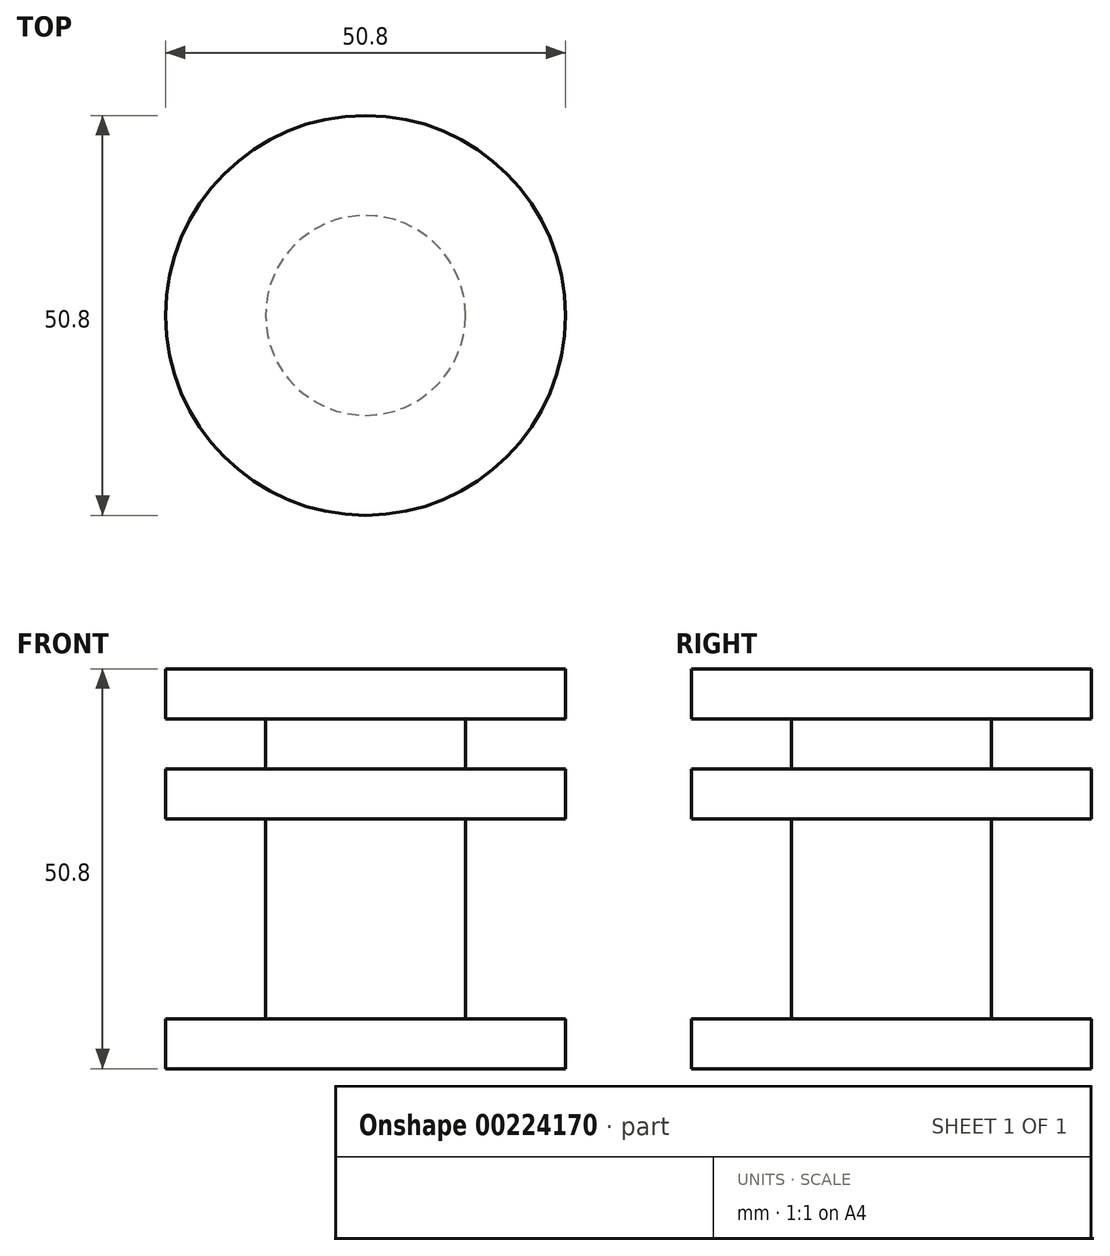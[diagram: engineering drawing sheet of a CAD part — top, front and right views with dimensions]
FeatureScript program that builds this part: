
annotation { "Feature Type Name" : "Feature", "Feature Type Description" : "" }
export const myFeature = defineFeature(function(context is Context, id is Id, definition is map)
    precondition{}
    {
        {
            var Q0;
            Q0=qCreatedBy(makeId("Front.planeOp"),FACE);
            var sketch = newSketch(context, id + "F0", { "sketchPlane" : qUnion([Q0])});
            skLineSegment(sketch, "E0", {"start": v(0, 0) * mm, "end": v(0, 47.13) * mm, "construction": true});
            skLineSegment(sketch, "E1", {"start": v(12.7, 0) * mm, "end": v(12.7, -25.4) * mm});
            skLineSegment(sketch, "E2", {"start": v(0, -25.4) * mm, "end": v(0, 0) * mm});
            skLineSegment(sketch, "E3", {"start": v(12.7, 0) * mm, "end": v(25.4, 0) * mm});
            skLineSegment(sketch, "E4", {"start": v(25.4, 0) * mm, "end": v(25.4, 6.35) * mm});
            skLineSegment(sketch, "E5", {"start": v(25.4, 6.35) * mm, "end": v(12.7, 6.35) * mm});
            skLineSegment(sketch, "E6", {"start": v(12.7, 6.35) * mm, "end": v(12.7, 12.7) * mm});
            skLineSegment(sketch, "E7", {"start": v(12.7, 12.7) * mm, "end": v(25.4, 12.7) * mm});
            skLineSegment(sketch, "E8", {"start": v(25.4, 12.7) * mm, "end": v(25.4, 19.05) * mm});
            skLineSegment(sketch, "E9", {"start": v(25.4, 19.05) * mm, "end": v(0, 19.05) * mm});
            skLineSegment(sketch, "E10", {"start": v(0, 19.05) * mm, "end": v(0, 0) * mm});
            skLineSegment(sketch, "E11", {"start": v(12.7, -25.4) * mm, "end": v(25.4, -25.4) * mm});
            skLineSegment(sketch, "E12", {"start": v(25.4, -25.4) * mm, "end": v(25.4, -31.75) * mm});
            skLineSegment(sketch, "E13", {"start": v(25.4, -31.75) * mm, "end": v(0, -31.75) * mm});
            skLineSegment(sketch, "E14", {"start": v(0, -31.75) * mm, "end": v(0, -25.4) * mm});
            skPoint(sketch, "E15.orphan", {"position": v(0, 6.35) * mm});
            skSolve(sketch);
        }
        {
            var Q0;
            Q0 = qSketchRegion(id + "F0", true);
            var Q1;
            Q1=sQuery(id+"F0.wireOp",EDGE,"E0");
            revolve(context, id + "F1", {"entities" : qUnion([Q0]), "axis" : qUnion([Q1]), "revolveType" : RevolveType.FULL});
        }
    });
